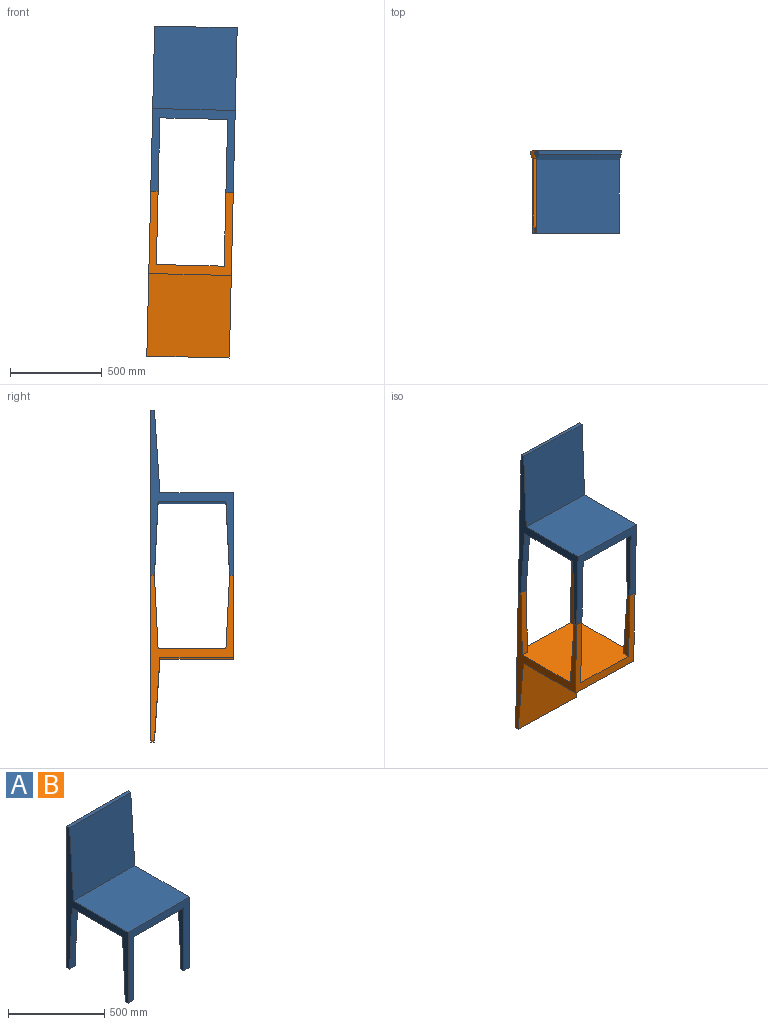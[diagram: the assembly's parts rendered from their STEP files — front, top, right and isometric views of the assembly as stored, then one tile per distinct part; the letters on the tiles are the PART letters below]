
ASSEMBLY  parts=2 mates=1
PART A: 20 faces, bbox 450x450x900 mm
  f0: plane 900x450mm, normal (-1,0,0), area 62250mm2, adj f2,f5,f7,f8,f9,f11,f14,f16
  f1: plane 900x450mm, normal (1,0,0), area 62250mm2, adj f2,f6,f7,f8,f9,f13,f14,f15
  f2: plane 450x450mm, normal (0,-1,0), area 54500mm2, adj f0,f1,f3,f4,f9,f11,f13,f19
  f3: plane 400x40mm, normal (1,0,0), area 12000mm2, adj f2,f9,f11,f18
  f4: plane 400x40mm, normal (-1,0,0), area 12000mm2, adj f2,f9,f13,f17
  f5: plane 40x20mm, normal (0,0,-1), area 800mm2, adj f0,f8,f10,f16
  f6: plane 40x20mm, normal (0,0,-1), area 800mm2, adj f1,f8,f12,f15
  f7: plane 450x20mm, normal (0,0,1), area 9000mm2, adj f0,f1,f8,f14
  f8: plane 900x450mm, normal (0,1,0), area 257000mm2, adj f0,f1,f5,f6,f7,f9,f10,f12
  f9: plane 450x450mm, normal (0,0,-1), area 196100mm2, adj f0,f1,f2,f3,f4,f8,f10,f12
  f10: plane 400x40mm, normal (1,0,0), area 12000mm2, adj f5,f8,f9,f16
  f11: plane 40x20mm, normal (0,0,-1), area 800mm2, adj f0,f2,f3,f18
  f12: plane 400x40mm, normal (-1,0,0), area 12000mm2, adj f6,f8,f9,f15
  f13: plane 40x20mm, normal (0,0,-1), area 800mm2, adj f1,f2,f4,f17
  f14: plane 450x450mm, normal (0,-1,0.07), area 202949.5mm2, adj f0,f1,f7,f19
  f15: plane 400x40mm, normal (0,-1,-0.05), area 16020mm2, adj f1,f6,f9,f12
  f16: plane 400x40mm, normal (0,-1,-0.05), area 16020mm2, adj f0,f5,f9,f10
  f17: plane 400x40mm, normal (0,1,-0.05), area 16020mm2, adj f1,f4,f9,f13
  f18: plane 400x40mm, normal (0,1,-0.05), area 16020mm2, adj f0,f3,f9,f11
  f19: plane 450x400mm, normal (0,0,1), area 180000mm2, adj f0,f1,f2,f14
PART B: same geometry as A
PLACE A rot(axis=(0,1,0),1.4deg) t=(-127.48,943.86,-330.88)mm
PLACE B rot(axis=(0,-1,0),178.6deg) t=(303.37,943.86,-1141.35)mm
MATE fastened B.f5 <-> A.f6  axis (0.02,0,1) through (292.89,1383.86,-740.99)mm
